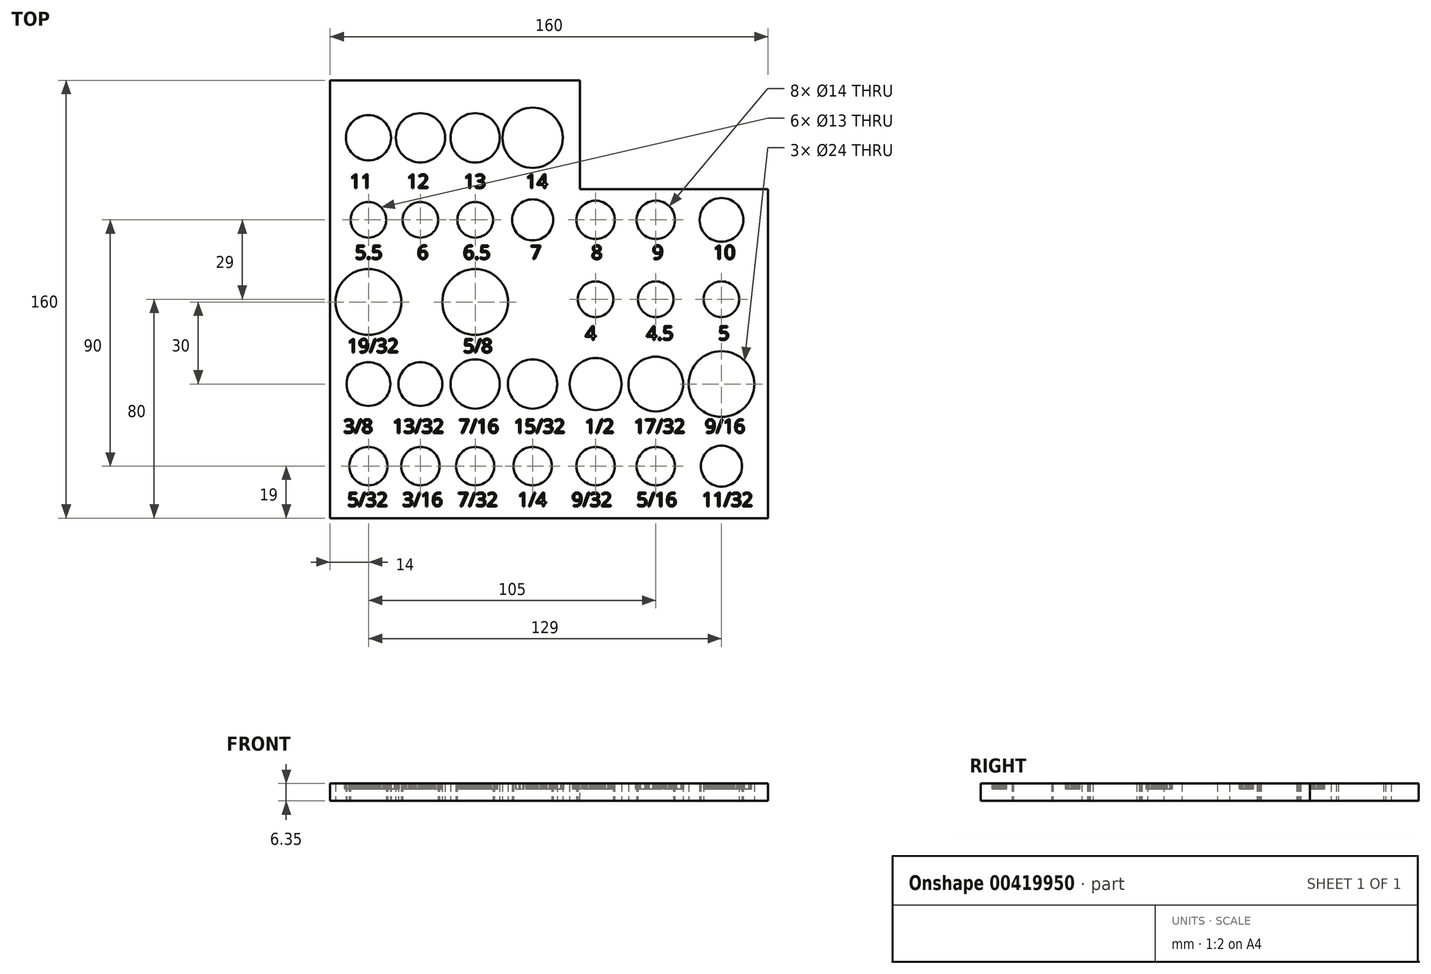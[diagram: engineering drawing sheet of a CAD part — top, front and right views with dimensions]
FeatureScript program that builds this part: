
annotation { "Feature Type Name" : "Feature", "Feature Type Description" : "" }
export const myFeature = defineFeature(function(context is Context, id is Id, definition is map)
    precondition{}
    {
        {
            var Q0;
            Q0=qCreatedBy(makeId("Top.planeOp"),FACE);
            var sketch = newSketch(context, id + "F0", { "sketchPlane" : qUnion([Q0])});
            skLineSegment(sketch, "E0.bottom", {"start": v(80, 80) * mm, "end": v(-80, 80) * mm});
            skLineSegment(sketch, "E0.top", {"start": v(80, -80) * mm, "end": v(-80, -80) * mm});
            skLineSegment(sketch, "E0.left", {"start": v(80, 80) * mm, "end": v(80, -80) * mm});
            skLineSegment(sketch, "E0.right", {"start": v(-80, 80) * mm, "end": v(-80, -80) * mm});
            skPoint(sketch, "E0.middle", {"position": v(0, 0) * mm});
            skLineSegment(sketch, "E1", {"start": v(-80, -61) * mm, "end": v(80, -61) * mm, "construction": true});
            skLineSegment(sketch, "E2", {"start": v(-80, -31) * mm, "end": v(80, -31) * mm, "construction": true});
            skLineSegment(sketch, "E3", {"start": v(-80, -1) * mm, "end": v(80, -1) * mm, "construction": true});
            skCircle(sketch, "E4", {"center": v(-66, -61) * mm, "radius": 7 * mm});
            skCircle(sketch, "E5", {"center": v(-47, -61) * mm, "radius": 7 * mm});
            skCircle(sketch, "E6", {"center": v(-27, -61) * mm, "radius": 7 * mm});
            skCircle(sketch, "E7", {"center": v(-6, -61) * mm, "radius": 7 * mm});
            skCircle(sketch, "E8", {"center": v(-66, -31) * mm, "radius": 8 * mm});
            skCircle(sketch, "E9", {"center": v(-47, -31) * mm, "radius": 8 * mm});
            skCircle(sketch, "E10", {"center": v(-27, -31) * mm, "radius": 9 * mm});
            skCircle(sketch, "E11", {"center": v(-6, -31) * mm, "radius": 9 * mm});
            skCircle(sketch, "E12", {"center": v(-66, -1) * mm, "radius": 12 * mm});
            skCircle(sketch, "E13", {"center": v(-27, -1) * mm, "radius": 12 * mm});
            skLineSegment(sketch, "E14", {"start": v(-80, 29) * mm, "end": v(80, 29) * mm, "construction": true});
            skCircle(sketch, "E15", {"center": v(-66, 29) * mm, "radius": 6.5 * mm});
            skCircle(sketch, "E16", {"center": v(-47, 29) * mm, "radius": 6.5 * mm});
            skCircle(sketch, "E17", {"center": v(-27, 29) * mm, "radius": 6.5 * mm});
            skCircle(sketch, "E18", {"center": v(-6, 29) * mm, "radius": 7.5 * mm});
            skLineSegment(sketch, "E19", {"start": v(-66, 80) * mm, "end": v(-66, -80) * mm, "construction": true});
            skLineSegment(sketch, "E20", {"start": v(-47, 80) * mm, "end": v(-47, -80) * mm, "construction": true});
            skLineSegment(sketch, "E21", {"start": v(-27, 80) * mm, "end": v(-27, -80) * mm, "construction": true});
            skLineSegment(sketch, "E22", {"start": v(-6, 80) * mm, "end": v(-6, -80) * mm, "construction": true});
            skLineSegment(sketch, "E23", {"start": v(17, 80) * mm, "end": v(17, -80) * mm, "construction": true});
            skLineSegment(sketch, "E24", {"start": v(39, 80) * mm, "end": v(39, -80) * mm, "construction": true});
            skLineSegment(sketch, "E25", {"start": v(63, 80) * mm, "end": v(63, -80) * mm, "construction": true});
            skCircle(sketch, "E26", {"center": v(17, -61) * mm, "radius": 7 * mm});
            skCircle(sketch, "E27", {"center": v(39, -61) * mm, "radius": 7 * mm});
            skCircle(sketch, "E28", {"center": v(63, -61) * mm, "radius": 7.5 * mm});
            skCircle(sketch, "E29", {"center": v(17, -31) * mm, "radius": 9.5 * mm});
            skPoint(sketch, "E29.centerSnap0", {"position": v(17, 0) * mm});
            skCircle(sketch, "E30", {"center": v(39, -31) * mm, "radius": 10 * mm});
            skCircle(sketch, "E31", {"center": v(63, -31) * mm, "radius": 12 * mm});
            skCircle(sketch, "E32", {"center": v(17, 0) * mm, "radius": 6.5 * mm});
            skCircle(sketch, "E33", {"center": v(39, 0) * mm, "radius": 6.5 * mm});
            skCircle(sketch, "E34", {"center": v(63, 0) * mm, "radius": 6.5 * mm});
            skCircle(sketch, "E35", {"center": v(17, 29) * mm, "radius": 7 * mm});
            skCircle(sketch, "E36", {"center": v(39, 29) * mm, "radius": 7 * mm});
            skCircle(sketch, "E37", {"center": v(63, 29) * mm, "radius": 8 * mm});
            skLineSegment(sketch, "E38", {"start": v(-80, 59) * mm, "end": v(80, 59) * mm, "construction": true});
            skCircle(sketch, "E39", {"center": v(-66, 59) * mm, "radius": 8.25 * mm});
            skCircle(sketch, "E40", {"center": v(-47, 59) * mm, "radius": 9 * mm});
            skCircle(sketch, "E41", {"center": v(-27, 59) * mm, "radius": 9 * mm});
            skCircle(sketch, "E42", {"center": v(-6, 59) * mm, "radius": 11 * mm});
            skSolve(sketch);
        }
        {
            var Q0;
            Q0=makeQuery(id+"F0.imprint","IMPRINT",FACE,{"disambiguationData":[TD([[makeQuery(id+"F0.imprint","IMPRINT",EDGE,{"derivedFrom":sQuery(id+"F0.wireOp",EDGE,"E0.bottom")}),1.0]])]});
            extrude(context, id + "F1", {"entities" : qUnion([Q0]), "depth" : (.25 * 25.4) * mm});
        }
        {
            var Q0;
            Q0=makeQuery(id+"F1.opExtrude","CAP_FACE",FACE,{"disambiguationData":[OSD([sQuery(id+"F0.wireOp",EDGE,"E0.bottom"),sQuery(id+"F0.wireOp",EDGE,"E0.top"),sQuery(id+"F0.wireOp",EDGE,"E0.left"),sQuery(id+"F0.wireOp",EDGE,"E0.right"),sQuery(id+"F0.wireOp",EDGE,"E4"),sQuery(id+"F0.wireOp",EDGE,"E5"),sQuery(id+"F0.wireOp",EDGE,"E6"),sQuery(id+"F0.wireOp",EDGE,"E7"),sQuery(id+"F0.wireOp",EDGE,"E8"),sQuery(id+"F0.wireOp",EDGE,"E9"),sQuery(id+"F0.wireOp",EDGE,"E10"),sQuery(id+"F0.wireOp",EDGE,"E11"),sQuery(id+"F0.wireOp",EDGE,"E12"),sQuery(id+"F0.wireOp",EDGE,"XrZT3hLZ-fSjp-fGqH-RahM-m9EaMsBtPWNb"),sQuery(id+"F0.wireOp",EDGE,"E13"),sQuery(id+"F0.wireOp",EDGE,"tyo6VUDq-6cDU-ZZHD-Gmyf-u5Ctohv65R71"),sQuery(id+"F0.wireOp",EDGE,"E15"),sQuery(id+"F0.wireOp",EDGE,"E16"),sQuery(id+"F0.wireOp",EDGE,"E17"),sQuery(id+"F0.wireOp",EDGE,"E18")])],"isStart":false});
            var sketch = newSketch(context, id + "F2", { "sketchPlane" : qUnion([Q0])});
            skText(sketch, "E43", { "text": "5/32   3/16   7/32    1/4     9/32     5/16     11/32", "fontName": "OpenSans-Regular.ttf"});
            skText(sketch, "E44", { "text": "3/8    13/32   7/16   15/32    1/2    17/32    9/16", "fontName": "OpenSans-Regular.ttf"});
            skText(sketch, "E45", { "text": "19/32             5/8  ", "fontName": "OpenSans-Regular.ttf"});
            skText(sketch, "E46", { "text": "4          4.5         5", "fontName": "OpenSans-Regular.ttf"});
            skText(sketch, "E47", { "text": "5.5       6       6.5        7          8          9          10", "fontName": "OpenSans-Regular.ttf"});
            skText(sketch, "E48", { "text": "11       12       13        14", "fontName": "OpenSans-Regular.ttf"});
            const initialGuessF2  = {"E43": [-0.07364, -0.0757, 1, 0, 0.00506], "E44": [-0.07505, -0.04889, 1, 0, 0.00506], "E45": [-0.07372, -0.0195, 1, 0, 0.00506], "E46": [0.01322, -0.01487, 1, 0, 0.00506], "E47": [-0.07086, 0.01466, 1, 0, 0.00506], "E48": [-0.07279, 0.0406, 1, 0, 0.00506]};
            skSetInitialGuess(sketch, initialGuessF2);
            skSolve(sketch);
        }
        {
            var Q0;
            Q0 = qSketchRegion(id + "F2", true);
            extrude(context, id + "F3", {"entities" : qUnion([Q0]), "operationType" : NewBodyOperationType.REMOVE, "oppositeDirection" : true, "depth" : 2 * mm});
        }
        {
            var Q0;
            {var subQ0=sQuery(id+"F0.wireOp",EDGE,"E42");var subQ1=sQuery(id+"F0.wireOp",EDGE,"E37");var subQ2=sQuery(id+"F0.wireOp",EDGE,"E41");var subQ3=sQuery(id+"F0.wireOp",EDGE,"E12");var subQ4=sQuery(id+"F0.wireOp",EDGE,"E13");var subQ5=sQuery(id+"F0.wireOp",EDGE,"E0.bottom");var subQ6=sQuery(id+"F0.wireOp",EDGE,"E0.top");var subQ7=sQuery(id+"F0.wireOp",EDGE,"E0.left");var subQ8=sQuery(id+"F0.wireOp",EDGE,"E0.right");var subQ9=sQuery(id+"F0.wireOp",EDGE,"E4");var subQ10=sQuery(id+"F0.wireOp",EDGE,"E5");var subQ11=sQuery(id+"F0.wireOp",EDGE,"E6");var subQ12=sQuery(id+"F0.wireOp",EDGE,"E7");var subQ13=sQuery(id+"F0.wireOp",EDGE,"E8");var subQ14=sQuery(id+"F0.wireOp",EDGE,"E9");var subQ15=sQuery(id+"F0.wireOp",EDGE,"E10");var subQ16=sQuery(id+"F0.wireOp",EDGE,"E11");var subQ17=sQuery(id+"F0.wireOp",EDGE,"E15");var subQ18=sQuery(id+"F0.wireOp",EDGE,"E16");var subQ19=sQuery(id+"F0.wireOp",EDGE,"E17");var subQ20=sQuery(id+"F0.wireOp",EDGE,"E18");var subQ21=sQuery(id+"F0.wireOp",EDGE,"E26");var subQ22=sQuery(id+"F0.wireOp",EDGE,"E27");var subQ23=sQuery(id+"F0.wireOp",EDGE,"E28");var subQ24=sQuery(id+"F0.wireOp",EDGE,"E29");var subQ25=sQuery(id+"F0.wireOp",EDGE,"E30");var subQ26=sQuery(id+"F0.wireOp",EDGE,"E31");var subQ27=sQuery(id+"F0.wireOp",EDGE,"E32");var subQ28=sQuery(id+"F0.wireOp",EDGE,"E33");var subQ29=sQuery(id+"F0.wireOp",EDGE,"E34");var subQ30=sQuery(id+"F0.wireOp",EDGE,"E35");var subQ31=sQuery(id+"F0.wireOp",EDGE,"E36");var subQ32=sQuery(id+"F0.wireOp",EDGE,"E39");var subQ33=sQuery(id+"F0.wireOp",EDGE,"E40");Q0=makeQuery(id+"F3.boolean.opBoolean","SPLIT",FACE,{"disambiguationData":[TD([makeQuery(id+"F1.opExtrude","SWEPT_FACE",FACE,{"disambiguationData":[OSD([subQ5])]})])],"derivedFrom":makeQuery(id+"F1.opExtrude","CAP_FACE",FACE,{"disambiguationData":[OSD([subQ5,subQ6,subQ7,subQ8,subQ9,subQ10,subQ11,subQ12,subQ13,subQ14,subQ15,subQ16,subQ3,subQ4,subQ17,subQ18,subQ19,subQ20,subQ21,subQ22,subQ23,subQ24,subQ25,subQ26,subQ27,subQ28,subQ29,subQ30,subQ31,subQ1,subQ32,subQ33,subQ2,subQ0])],"isStart":false})});}
            var sketch = newSketch(context, id + "F4", { "sketchPlane" : qUnion([Q0])});
            skLineSegment(sketch, "E49.bottom", {"start": v(11.32, 80) * mm, "end": v(80, 80) * mm});
            skLineSegment(sketch, "E49.top", {"start": v(11.32, 40.28) * mm, "end": v(80, 40.28) * mm});
            skLineSegment(sketch, "E49.left", {"start": v(11.32, 80) * mm, "end": v(11.32, 40.28) * mm});
            skLineSegment(sketch, "E49.right", {"start": v(80, 80) * mm, "end": v(80, 40.28) * mm});
            skSolve(sketch);
        }
        {
            var Q0;
            Q0 = qSketchRegion(id + "F4", true);
            var Q1;
            Q1=makeQuery(id+"F1.opExtrude","CAP_FACE",FACE,{"disambiguationData":[OSD([sQuery(id+"F0.wireOp",EDGE,"E0.bottom"),sQuery(id+"F0.wireOp",EDGE,"E0.top"),sQuery(id+"F0.wireOp",EDGE,"E0.left"),sQuery(id+"F0.wireOp",EDGE,"E0.right"),sQuery(id+"F0.wireOp",EDGE,"E4"),sQuery(id+"F0.wireOp",EDGE,"E5"),sQuery(id+"F0.wireOp",EDGE,"E6"),sQuery(id+"F0.wireOp",EDGE,"E7"),sQuery(id+"F0.wireOp",EDGE,"E8"),sQuery(id+"F0.wireOp",EDGE,"E9"),sQuery(id+"F0.wireOp",EDGE,"E10"),sQuery(id+"F0.wireOp",EDGE,"E11"),sQuery(id+"F0.wireOp",EDGE,"E12"),sQuery(id+"F0.wireOp",EDGE,"E13"),sQuery(id+"F0.wireOp",EDGE,"E15"),sQuery(id+"F0.wireOp",EDGE,"E16"),sQuery(id+"F0.wireOp",EDGE,"E17"),sQuery(id+"F0.wireOp",EDGE,"E18"),sQuery(id+"F0.wireOp",EDGE,"E26"),sQuery(id+"F0.wireOp",EDGE,"E27"),sQuery(id+"F0.wireOp",EDGE,"E28"),sQuery(id+"F0.wireOp",EDGE,"E29"),sQuery(id+"F0.wireOp",EDGE,"E30"),sQuery(id+"F0.wireOp",EDGE,"E31"),sQuery(id+"F0.wireOp",EDGE,"E32"),sQuery(id+"F0.wireOp",EDGE,"E33"),sQuery(id+"F0.wireOp",EDGE,"E34"),sQuery(id+"F0.wireOp",EDGE,"E35"),sQuery(id+"F0.wireOp",EDGE,"E36"),sQuery(id+"F0.wireOp",EDGE,"E37"),sQuery(id+"F0.wireOp",EDGE,"E39"),sQuery(id+"F0.wireOp",EDGE,"E40"),sQuery(id+"F0.wireOp",EDGE,"E41"),sQuery(id+"F0.wireOp",EDGE,"E42")])],"isStart":true});
            extrude(context, id + "F5", {"entities" : qUnion([Q0]), "operationType" : NewBodyOperationType.REMOVE, "endBound" : BoundingType.UP_TO_SURFACE, "oppositeDirection" : true, "endBoundEntityFace" : qUnion([Q1]), "depth" : 25 * mm});
        }
    });
